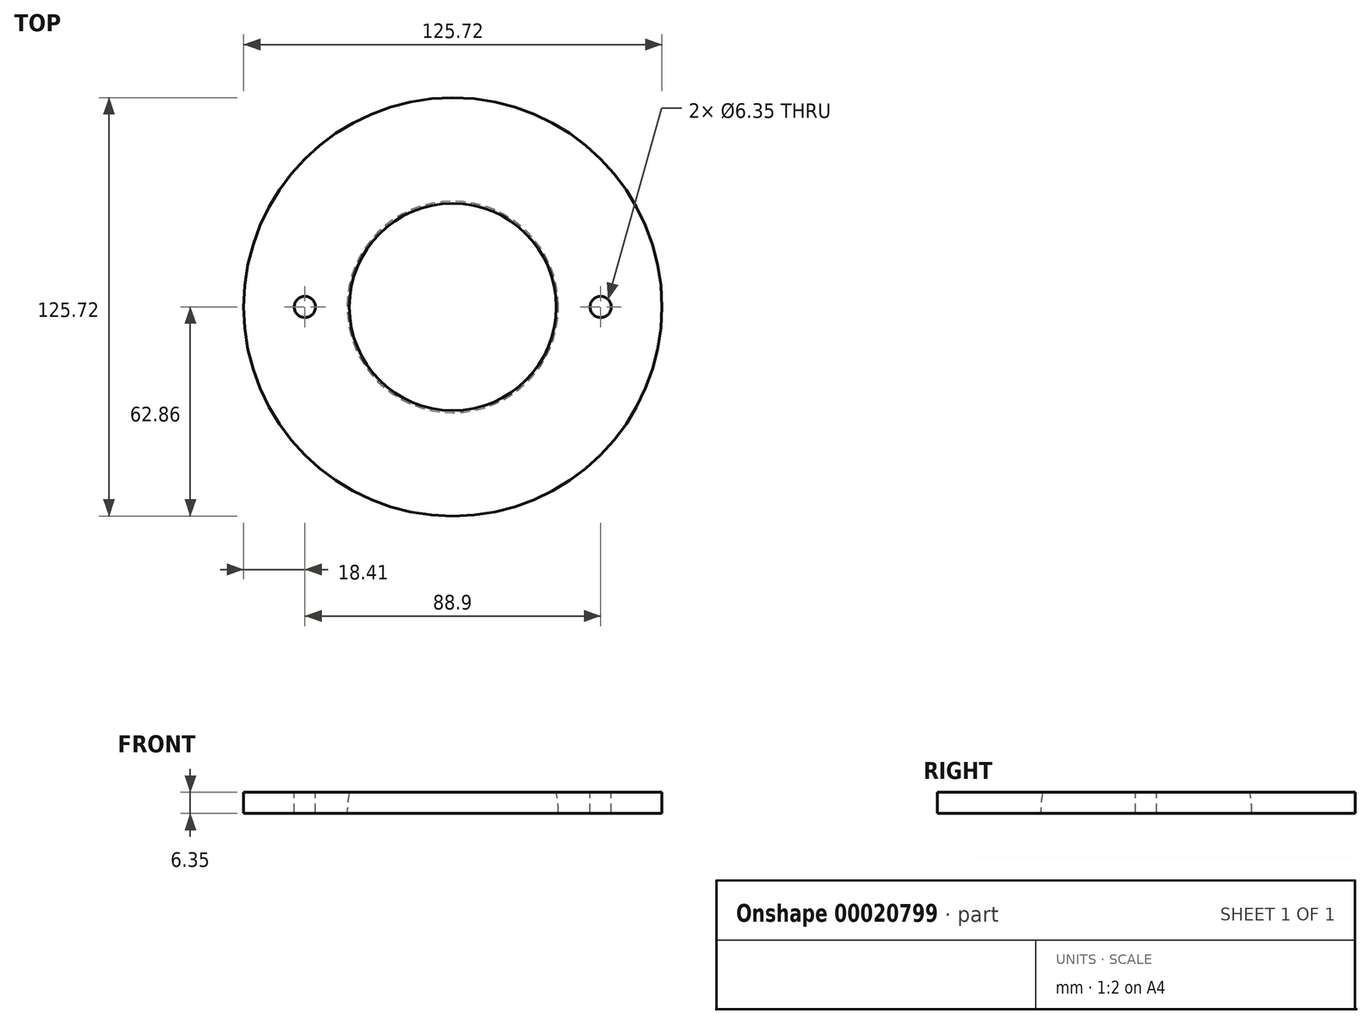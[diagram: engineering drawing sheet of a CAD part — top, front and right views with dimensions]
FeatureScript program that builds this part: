
annotation { "Feature Type Name" : "Feature", "Feature Type Description" : "" }
export const myFeature = defineFeature(function(context is Context, id is Id, definition is map)
    precondition{}
    {
        {
            var Q0;
            Q0=qCreatedBy(makeId("Front.planeOp"),FACE);
            var sketch = newSketch(context, id + "F0", { "sketchPlane" : qUnion([Q0])});
            skLineSegment(sketch, "E0.rect.top", {"start": v(-31.1, 6.35) * mm, "end": v(-62.86, 6.35) * mm});
            skLineSegment(sketch, "E0.rect.right", {"start": v(-62.86, 0) * mm, "end": v(-62.86, 6.35) * mm});
            skPoint(sketch, "E0.rect.middle", {"position": v(0, 0) * mm});
            skArc(sketch, "E1", {"start": v(-31.1, 6.35) * mm, "mid": v(-31.75, 0) * mm, "end": v(-31.1, -6.35) * mm});
            skLineSegment(sketch, "E2", {"start": v(-31.75, 0) * mm, "end": v(-62.86, 0) * mm});
            skLineSegment(sketch, "E3", {"start": v(0, 0) * mm, "end": v(0, -24.74) * mm, "construction": true});
            skLineSegment(sketch, "E4.MirrorCS", {"start": v(-31.1, -6.35) * mm, "end": v(-62.86, -6.35) * mm});
            skLineSegment(sketch, "E5.MirrorCS", {"start": v(-62.86, 0) * mm, "end": v(-62.86, -6.35) * mm});
            skSolve(sketch);
        }
        {
            var Q0;
            {var subQ2=sQuery(id+"F0.wireOp",EDGE,"E0.rect.top");Q0=makeQuery(id+"F0.imprint","IMPRINT",FACE,{"disambiguationData":[TD([[makeQuery(id+"F0.imprint","IMPRINT",EDGE,{"derivedFrom":subQ2}),1.0]])]});}
            var Q1;
            Q1=sQuery(id+"F0.wireOp",EDGE,"E3");
            revolve(context, id + "F1", {"entities" : qUnion([Q0]), "axis" : qUnion([Q1]), "revolveType" : RevolveType.FULL});
        }
        {
            var Q0;
            Q0=makeQuery(id+"F1.opRevolve","SWEPT_FACE",FACE,{"disambiguationData":[OSD([sQuery(id+"F0.wireOp",EDGE,"E0.rect.top")])]});
            var sketch = newSketch(context, id + "F2", { "sketchPlane" : qUnion([Q0])});
            skCircle(sketch, "E6", {"center": v(-44.45, 0) * mm, "radius": 3.18 * mm});
            skCircle(sketch, "E7", {"center": v(44.45, 0) * mm, "radius": 3.18 * mm});
            skSolve(sketch);
        }
        {
            var Q0;
            Q0 = qSketchRegion(id + "F2", true);
            extrude(context, id + "F3", {"entities" : qUnion([Q0]), "operationType" : NewBodyOperationType.REMOVE, "endBound" : BoundingType.THROUGH_ALL, "oppositeDirection" : true, "depth" : 25.4 * mm});
        }
    });
